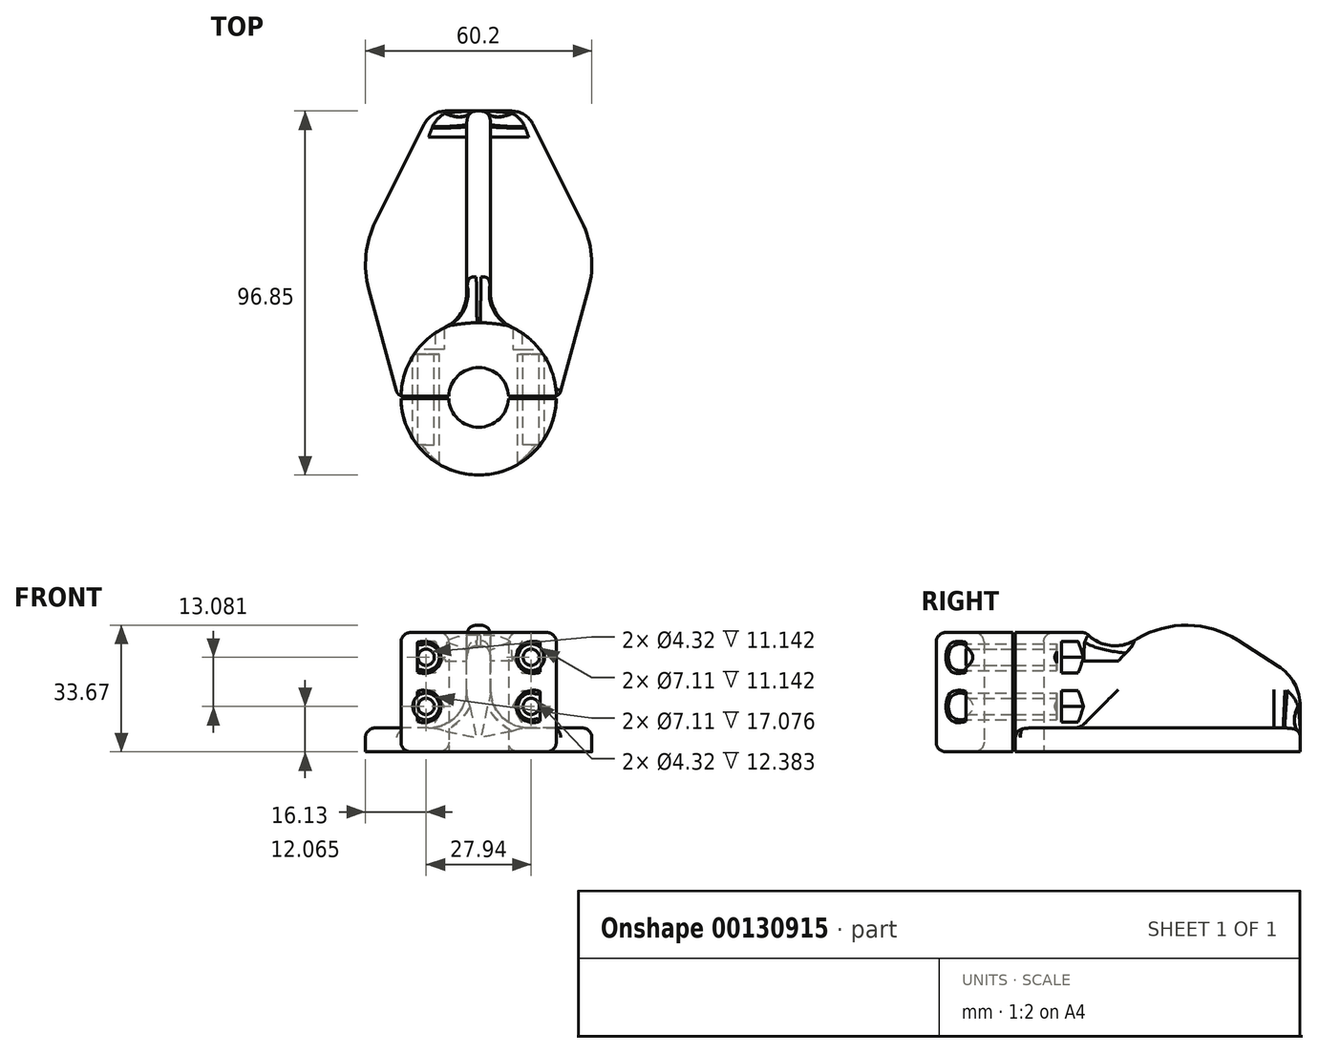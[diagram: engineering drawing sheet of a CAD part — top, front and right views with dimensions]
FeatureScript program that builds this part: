
annotation { "Feature Type Name" : "Feature", "Feature Type Description" : "" }
export const myFeature = defineFeature(function(context is Context, id is Id, definition is map)
    precondition{}
    {
        {
            var Q0;
            Q0=qCreatedBy(makeId("Top.planeOp"),FACE);
            var sketch = newSketch(context, id + "F0", { "sketchPlane" : qUnion([Q0])});
            skArc(sketch, "E0", {"start": v(-7.94, -0.32) * mm, "mid": v(0, -7.95) * mm, "end": v(7.94, -0.32) * mm});
            skLineSegment(sketch, "E1", {"start": v(51.79, -19.76) * mm, "end": v(0, -19.76) * mm});
            skLineSegment(sketch, "E2.MirrorCS", {"start": v(-51.79, -19.76) * mm, "end": v(0, -19.76) * mm});
            skArc(sketch, "E3", {"start": v(-20.65, -0.32) * mm, "mid": v(0, -20.65) * mm, "end": v(20.65, -0.32) * mm});
            skLineSegment(sketch, "E4", {"start": v(0, 76.2) * mm, "end": v(8.78, 76.2) * mm});
            skLineSegment(sketch, "E5", {"start": v(14.46, 72.69) * mm, "end": v(27.42, 46.77) * mm});
            skLineSegment(sketch, "E6", {"start": v(29.2, 28.75) * mm, "end": v(21.87, 1.72) * mm});
            skLineSegment(sketch, "E7", {"start": v(0, -19.76) * mm, "end": v(0, -61.3) * mm});
            skLineSegment(sketch, "E8.MirrorCS", {"start": v(0, 76.2) * mm, "end": v(-8.78, 76.2) * mm});
            skLineSegment(sketch, "E9.MirrorCS", {"start": v(-29.2, 28.75) * mm, "end": v(-21.87, 1.72) * mm});
            skLineSegment(sketch, "E10.MirrorCS", {"start": v(-14.46, 72.69) * mm, "end": v(-27.42, 46.77) * mm});
            skPoint(sketch, "E11.visualSharp", {"position": v(31.75, 38.1) * mm});
            skArc(sketch, "E11.filletArc", {"start": v(29.2, 28.75) * mm, "mid": v(29.97, 37.92) * mm, "end": v(27.42, 46.77) * mm});
            skPoint(sketch, "E12.visualSharp", {"position": v(-31.75, 38.1) * mm});
            skArc(sketch, "E12.filletArc", {"start": v(-27.42, 46.77) * mm, "mid": v(-29.97, 37.92) * mm, "end": v(-29.2, 28.75) * mm});
            skPoint(sketch, "E13.visualSharp", {"position": v(12.7, 76.2) * mm});
            skArc(sketch, "E13.filletArc", {"start": v(14.46, 72.69) * mm, "mid": v(12.11, 75.25) * mm, "end": v(8.78, 76.2) * mm});
            skPoint(sketch, "E14.visualSharp", {"position": v(-12.7, 76.2) * mm});
            skArc(sketch, "E14.filletArc", {"start": v(-8.78, 76.2) * mm, "mid": v(-12.11, 75.25) * mm, "end": v(-14.46, 72.69) * mm});
            skLineSegment(sketch, "E15", {"start": v(-24.66, 0) * mm, "end": v(25.12, 0) * mm});
            skLineSegment(sketch, "E16.0", {"start": v(-20.65, -0.32) * mm, "end": v(20.65, -0.32) * mm});
            skLineSegment(sketch, "E17.0", {"start": v(-20.03, 0.32) * mm, "end": v(20.03, 0.32) * mm});
            skArc(sketch, "E18.trimOffspring", {"start": v(7.94, 0.32) * mm, "mid": v(0, 7.95) * mm, "end": v(-7.94, 0.32) * mm});
            skArc(sketch, "E19.trimOffspring", {"start": v(20.65, 0.32) * mm, "mid": v(0, 20.65) * mm, "end": v(-20.65, 0.32) * mm});
            skPoint(sketch, "E20.visualSharp", {"position": v(-21.49, 0.32) * mm});
            skArc(sketch, "E20.filletArc", {"start": v(-21.87, 1.72) * mm, "mid": v(-21.19, 0.7) * mm, "end": v(-20.03, 0.32) * mm});
            skPoint(sketch, "E21.visualSharp", {"position": v(21.49, 0.32) * mm});
            skArc(sketch, "E21.filletArc", {"start": v(20.03, 0.32) * mm, "mid": v(21.19, 0.7) * mm, "end": v(21.87, 1.72) * mm});
            skSolve(sketch);
        }
        {
            var Q0;
            Q0=qCreatedBy(makeId("Right.planeOp"),FACE);
            var sketch = newSketch(context, id + "F1", { "sketchPlane" : qUnion([Q0])});
            skLineSegment(sketch, "E22", {"start": v(-14.29, 0) * mm, "end": v(-14.29, 19.05) * mm});
            skLineSegment(sketch, "E23", {"start": v(-14.29, 0) * mm, "end": v(76.2, 0) * mm});
            skPoint(sketch, "E24.visualSharp", {"position": v(46.35, 38.1) * mm});
            skLineSegment(sketch, "E25", {"start": v(76.2, 0) * mm, "end": v(76.2, 12.09) * mm});
            skLineSegment(sketch, "E26", {"start": v(70.33, 22.8) * mm, "end": v(59.54, 29.68) * mm});
            skLineSegment(sketch, "E27", {"start": v(-14.29, 19.05) * mm, "end": v(7.31, 19.05) * mm});
            skLineSegment(sketch, "E28", {"start": v(20.28, 22.61) * mm, "end": v(32.9, 30.1) * mm});
            skPoint(sketch, "E29.visualSharp", {"position": v(14.29, 19.05) * mm});
            skArc(sketch, "E29.filletArc", {"start": v(7.31, 19.05) * mm, "mid": v(14.04, 19.96) * mm, "end": v(20.28, 22.61) * mm});
            skPoint(sketch, "E30.visualSharp", {"position": v(46.36, 38.1) * mm});
            skArc(sketch, "E30.filletArc", {"start": v(59.54, 29.68) * mm, "mid": v(46.28, 33.67) * mm, "end": v(32.9, 30.1) * mm});
            skLineSegment(sketch, "E31", {"start": v(6.35, 0) * mm, "end": v(6.35, 19.05) * mm});
            skPoint(sketch, "E32.visualSharp", {"position": v(76.2, 19.05) * mm});
            skArc(sketch, "E32.filletArc", {"start": v(76.2, 12.09) * mm, "mid": v(74.64, 18.2) * mm, "end": v(70.33, 22.8) * mm});
            skSolve(sketch);
        }
        {
            var Q0;
            Q0=makeQuery(id+"F0.imprint","IMPRINT",FACE,{"disambiguationData":[TD([[makeQuery(id+"F0.imprint","IMPRINT",EDGE,{"derivedFrom":sQuery(id+"F0.wireOp",EDGE,"E0")}),-1.0]])]});
            var Q1;
            {var subQ1=sQuery(id+"F0.wireOp",EDGE,"E1");var subQ3=sQuery(id+"F0.wireOp",EDGE,"E3");var subQ4=makeQuery(id+"F0.imprint","INTERSECT",VERTEX,{"derivedFrom":[subQ1,subQ3]});Q1=makeQuery(id+"F0.imprint","IMPRINT",FACE,{"disambiguationData":[TD([[makeQuery(id+"F0.imprint","IMPRINT",EDGE,{"disambiguationData":[TD([[subQ4,1.0]])],"derivedFrom":subQ3}),1.0]])]});}
            var Q2;
            {var subQ1=sQuery(id+"F0.wireOp",EDGE,"E2.MirrorCS");var subQ3=sQuery(id+"F0.wireOp",EDGE,"E3");var subQ4=makeQuery(id+"F0.imprint","INTERSECT",VERTEX,{"derivedFrom":[subQ1,subQ3]});Q2=makeQuery(id+"F0.imprint","IMPRINT",FACE,{"disambiguationData":[TD([[makeQuery(id+"F0.imprint","IMPRINT",EDGE,{"disambiguationData":[TD([[subQ4,-1.0]])],"derivedFrom":subQ3}),1.0]])]});}
            extrude(context, id + "F2", {"entities" : qUnion([Q0, Q1, Q2]), "depth" : 31.75 * mm});
        }
        {
            var Q0;
            Q0=makeQuery(id+"F0.imprint","IMPRINT",FACE,{"disambiguationData":[TD([[makeQuery(id+"F0.imprint","IMPRINT",EDGE,{"derivedFrom":sQuery(id+"F0.wireOp",EDGE,"E4")}),-1.0]])]});
            extrude(context, id + "F3", {"entities" : qUnion([Q0]), "depth" : 6.35 * mm});
        }
        {
            var Q0;
            {var subQ3=sQuery(id+"F1.wireOp",EDGE,"E25");Q0=makeQuery(id+"F1.imprint","IMPRINT",FACE,{"disambiguationData":[TD([[makeQuery(id+"F1.imprint","IMPRINT",EDGE,{"derivedFrom":subQ3}),1.0]])]});}
            extrude(context, id + "F4", {"entities" : qUnion([Q0]), "depth" : 3.17 * mm, "hasSecondDirection" : true, "secondDirectionOppositeDirection" : true, "secondDirectionDepth" : 3.17 * mm});
        }
        {
            var Q0;
            {var subQ0=sQuery(id+"F0.wireOp",EDGE,"E18.trimOffspring");Q0=makeQuery(id+"F0.imprint","IMPRINT",FACE,{"disambiguationData":[TD([[makeQuery(id+"F0.imprint","IMPRINT",EDGE,{"derivedFrom":subQ0}),-1.0]])]});}
            extrude(context, id + "F5", {"entities" : qUnion([Q0]), "depth" : 31.75 * mm});
        }
        {
            var Q0;
            Q0=qCreatedBy(makeId("Front.planeOp"),FACE);
            var sketch = newSketch(context, id + "F6", { "sketchPlane" : qUnion([Q0])});
            skCircle(sketch, "E33", {"center": v(13.97, 12.07) * mm, "radius": 3.56 * mm});
            skCircle(sketch, "E34.cCircle", {"center": v(13.97, 12.07) * mm, "radius": 4.2 * mm, "construction": true});
            skLineSegment(sketch, "E34.0", {"start": v(11.55, 16.26) * mm, "end": v(16.39, 16.26) * mm});
            skLineSegment(sketch, "E34.1", {"start": v(16.39, 16.26) * mm, "end": v(18.8, 12.07) * mm});
            skLineSegment(sketch, "E34.2", {"start": v(18.8, 12.07) * mm, "end": v(16.39, 7.87) * mm});
            skLineSegment(sketch, "E34.3", {"start": v(16.39, 7.87) * mm, "end": v(11.55, 7.87) * mm});
            skLineSegment(sketch, "E34.4", {"start": v(11.55, 7.87) * mm, "end": v(9.13, 12.07) * mm});
            skLineSegment(sketch, "E34.5", {"start": v(9.13, 12.07) * mm, "end": v(11.55, 16.26) * mm});
            skPoint(sketch, "E34.0.midPoint", {"position": v(13.97, 16.26) * mm});
            skCircle(sketch, "E35", {"center": v(13.97, 12.07) * mm, "radius": 2.16 * mm});
            skLineSegment(sketch, "E36", {"start": v(0, 0) * mm, "end": v(0, 18.6) * mm});
            skLineSegment(sketch, "E37", {"start": v(0, 18.6) * mm, "end": v(28.99, 18.6) * mm});
            skPoint(sketch, "E38.MirrorP", {"position": v(13.97, 20.96) * mm});
            skLineSegment(sketch, "E39.MirrorCS", {"start": v(11.55, 29.34) * mm, "end": v(9.13, 25.15) * mm});
            skLineSegment(sketch, "E40.MirrorCS", {"start": v(16.39, 29.34) * mm, "end": v(11.55, 29.34) * mm});
            skLineSegment(sketch, "E41.MirrorCS", {"start": v(18.8, 25.15) * mm, "end": v(16.39, 29.34) * mm});
            skLineSegment(sketch, "E42.MirrorCS", {"start": v(11.55, 20.96) * mm, "end": v(16.39, 20.96) * mm});
            skLineSegment(sketch, "E43.MirrorCS", {"start": v(9.13, 25.15) * mm, "end": v(11.55, 20.96) * mm});
            skLineSegment(sketch, "E44.MirrorCS", {"start": v(16.39, 20.96) * mm, "end": v(18.8, 25.15) * mm});
            skCircle(sketch, "E45.MirrorC", {"center": v(13.97, 25.15) * mm, "radius": 2.16 * mm});
            skCircle(sketch, "E46.MirrorC", {"center": v(13.97, 25.15) * mm, "radius": 3.56 * mm});
            skCircle(sketch, "E47.MirrorC", {"center": v(13.97, 25.15) * mm, "radius": 4.2 * mm, "construction": true});
            skLineSegment(sketch, "E48.MirrorCS", {"start": v(-11.55, 16.26) * mm, "end": v(-16.39, 16.26) * mm});
            skLineSegment(sketch, "E49.MirrorCS", {"start": v(-16.39, 16.26) * mm, "end": v(-18.8, 12.07) * mm});
            skLineSegment(sketch, "E50.MirrorCS", {"start": v(-9.13, 25.15) * mm, "end": v(-11.55, 20.96) * mm});
            skCircle(sketch, "E51.MirrorC", {"center": v(-13.97, 25.15) * mm, "radius": 2.16 * mm});
            skCircle(sketch, "E52.MirrorC", {"center": v(-13.97, 25.15) * mm, "radius": 4.2 * mm, "construction": true});
            skLineSegment(sketch, "E53.MirrorCS", {"start": v(-16.39, 20.95) * mm, "end": v(-18.8, 25.15) * mm});
            skCircle(sketch, "E54.MirrorC", {"center": v(-13.97, 12.06) * mm, "radius": 2.16 * mm});
            skLineSegment(sketch, "E55.MirrorCS", {"start": v(-9.13, 12.07) * mm, "end": v(-11.55, 16.26) * mm});
            skLineSegment(sketch, "E56.MirrorCS", {"start": v(-11.55, 7.87) * mm, "end": v(-9.13, 12.06) * mm});
            skLineSegment(sketch, "E57.MirrorCS", {"start": v(-16.39, 7.87) * mm, "end": v(-11.55, 7.87) * mm});
            skCircle(sketch, "E58.MirrorC", {"center": v(-13.97, 12.06) * mm, "radius": 4.2 * mm, "construction": true});
            skPoint(sketch, "E59.MirrorP", {"position": v(-13.97, 16.26) * mm});
            skCircle(sketch, "E60.MirrorC", {"center": v(-13.97, 25.15) * mm, "radius": 3.56 * mm});
            skLineSegment(sketch, "E61.MirrorCS", {"start": v(-11.55, 29.34) * mm, "end": v(-9.13, 25.15) * mm});
            skLineSegment(sketch, "E62.MirrorCS", {"start": v(-18.8, 12.07) * mm, "end": v(-16.39, 7.87) * mm});
            skLineSegment(sketch, "E63.MirrorCS", {"start": v(-11.55, 20.96) * mm, "end": v(-16.39, 20.96) * mm});
            skPoint(sketch, "E64.MirrorP", {"position": v(-13.97, 20.96) * mm});
            skLineSegment(sketch, "E65.MirrorCS", {"start": v(-18.8, 25.15) * mm, "end": v(-16.39, 29.34) * mm});
            skLineSegment(sketch, "E66.MirrorCS", {"start": v(-16.39, 29.34) * mm, "end": v(-11.55, 29.34) * mm});
            skCircle(sketch, "E67.MirrorC", {"center": v(-13.97, 12.06) * mm, "radius": 3.56 * mm});
            skSolve(sketch);
        }
        {
            var Q0;
            Q0=makeQuery(id+"F6.imprint","IMPRINT",FACE,{"disambiguationData":[TD([[makeQuery(id+"F6.imprint","IMPRINT",EDGE,{"derivedFrom":sQuery(id+"F6.wireOp",EDGE,"E33")}),-1.0]])]});
            var Q1;
            Q1=makeQuery(id+"F6.imprint","IMPRINT",FACE,{"disambiguationData":[TD([[makeQuery(id+"F6.imprint","IMPRINT",EDGE,{"derivedFrom":sQuery(id+"F6.wireOp",EDGE,"E33")}),1.0]])]});
            var Q2;
            Q2=makeQuery(id+"F6.imprint","IMPRINT",FACE,{"disambiguationData":[TD([[makeQuery(id+"F6.imprint","IMPRINT",EDGE,{"derivedFrom":sQuery(id+"F6.wireOp",EDGE,"E35")}),1.0]])]});
            var Q3;
            Q3=makeQuery(id+"F6.imprint","IMPRINT",FACE,{"disambiguationData":[TD([[makeQuery(id+"F6.imprint","IMPRINT",EDGE,{"derivedFrom":sQuery(id+"F6.wireOp",EDGE,"E48.MirrorCS")}),1.0]])]});
            var Q4;
            Q4=makeQuery(id+"F6.imprint","IMPRINT",FACE,{"disambiguationData":[TD([[makeQuery(id+"F6.imprint","IMPRINT",EDGE,{"derivedFrom":sQuery(id+"F6.wireOp",EDGE,"E54.MirrorC")}),1.0]])]});
            var Q5;
            Q5=makeQuery(id+"F6.imprint","IMPRINT",FACE,{"disambiguationData":[TD([[makeQuery(id+"F6.imprint","IMPRINT",EDGE,{"derivedFrom":sQuery(id+"F6.wireOp",EDGE,"E54.MirrorC")}),-1.0]])]});
            var Q6;
            Q6=makeQuery(id+"F6.imprint","IMPRINT",FACE,{"disambiguationData":[TD([[makeQuery(id+"F6.imprint","IMPRINT",EDGE,{"derivedFrom":sQuery(id+"F6.wireOp",EDGE,"E50.MirrorCS")}),-1.0]])]});
            var Q7;
            Q7=makeQuery(id+"F6.imprint","IMPRINT",FACE,{"disambiguationData":[TD([[makeQuery(id+"F6.imprint","IMPRINT",EDGE,{"derivedFrom":sQuery(id+"F6.wireOp",EDGE,"E51.MirrorC")}),-1.0]])]});
            var Q8;
            Q8=makeQuery(id+"F6.imprint","IMPRINT",FACE,{"disambiguationData":[TD([[makeQuery(id+"F6.imprint","IMPRINT",EDGE,{"derivedFrom":sQuery(id+"F6.wireOp",EDGE,"E51.MirrorC")}),1.0]])]});
            var Q9;
            Q9=makeQuery(id+"F6.imprint","IMPRINT",FACE,{"disambiguationData":[TD([[makeQuery(id+"F6.imprint","IMPRINT",EDGE,{"derivedFrom":sQuery(id+"F6.wireOp",EDGE,"E39.MirrorCS")}),1.0]])]});
            var Q10;
            Q10=makeQuery(id+"F6.imprint","IMPRINT",FACE,{"disambiguationData":[TD([[makeQuery(id+"F6.imprint","IMPRINT",EDGE,{"derivedFrom":sQuery(id+"F6.wireOp",EDGE,"E45.MirrorC")}),1.0]])]});
            var Q11;
            Q11=makeQuery(id+"F6.imprint","IMPRINT",FACE,{"disambiguationData":[TD([[makeQuery(id+"F6.imprint","IMPRINT",EDGE,{"derivedFrom":sQuery(id+"F6.wireOp",EDGE,"E45.MirrorC")}),-1.0]])]});
            var Q12;
            Q12=makeQuery(id+"F6.imprint","IMPRINT",FACE,{"disambiguationData":[TD([[makeQuery(id+"F6.imprint","IMPRINT",EDGE,{"derivedFrom":sQuery(id+"F6.wireOp",EDGE,"E61.MirrorCS")}),1.0]])]});
            var Q13;
            Q13=makeQuery(id+"F6.imprint","IMPRINT",FACE,{"disambiguationData":[TD([[makeQuery(id+"F6.imprint","IMPRINT",EDGE,{"derivedFrom":sQuery(id+"F6.wireOp",EDGE,"E39.MirrorCS")}),-1.0]])]});
            var Q14;
            Q14=makeQuery(id+"F6.imprint","IMPRINT",FACE,{"disambiguationData":[TD([[makeQuery(id+"F6.imprint","IMPRINT",EDGE,{"derivedFrom":sQuery(id+"F6.wireOp",EDGE,"E34.0")}),1.0]])]});
            var Q15;
            Q15=makeQuery(id+"F6.imprint","IMPRINT",FACE,{"disambiguationData":[TD([[makeQuery(id+"F6.imprint","IMPRINT",EDGE,{"derivedFrom":sQuery(id+"F6.wireOp",EDGE,"E48.MirrorCS")}),-1.0]])]});
            extrude(context, id + "F7", {"entities" : qUnion([Q0, Q1, Q2, Q3, Q4, Q5, Q6, Q7, Q8, Q9, Q10, Q11, Q12, Q13, Q14, Q15]), "operationType" : NewBodyOperationType.REMOVE, "oppositeDirection" : true, "depth" : 30.43 * mm, "hasSecondDirection" : true, "secondDirectionOppositeDirection" : true, "secondDirectionDepth" : 12.7 * mm});
        }
        {
            var Q0;
            Q0=makeQuery(id+"F6.imprint","IMPRINT",FACE,{"disambiguationData":[TD([[makeQuery(id+"F6.imprint","IMPRINT",EDGE,{"derivedFrom":sQuery(id+"F6.wireOp",EDGE,"E33")}),1.0]])]});
            var Q1;
            Q1=makeQuery(id+"F6.imprint","IMPRINT",FACE,{"disambiguationData":[TD([[makeQuery(id+"F6.imprint","IMPRINT",EDGE,{"derivedFrom":sQuery(id+"F6.wireOp",EDGE,"E35")}),1.0]])]});
            var Q2;
            Q2=makeQuery(id+"F6.imprint","IMPRINT",FACE,{"disambiguationData":[TD([[makeQuery(id+"F6.imprint","IMPRINT",EDGE,{"derivedFrom":sQuery(id+"F6.wireOp",EDGE,"E54.MirrorC")}),1.0]])]});
            var Q3;
            Q3=makeQuery(id+"F6.imprint","IMPRINT",FACE,{"disambiguationData":[TD([[makeQuery(id+"F6.imprint","IMPRINT",EDGE,{"derivedFrom":sQuery(id+"F6.wireOp",EDGE,"E54.MirrorC")}),-1.0]])]});
            var Q4;
            Q4=makeQuery(id+"F6.imprint","IMPRINT",FACE,{"disambiguationData":[TD([[makeQuery(id+"F6.imprint","IMPRINT",EDGE,{"derivedFrom":sQuery(id+"F6.wireOp",EDGE,"E51.MirrorC")}),-1.0]])]});
            var Q5;
            Q5=makeQuery(id+"F6.imprint","IMPRINT",FACE,{"disambiguationData":[TD([[makeQuery(id+"F6.imprint","IMPRINT",EDGE,{"derivedFrom":sQuery(id+"F6.wireOp",EDGE,"E51.MirrorC")}),1.0]])]});
            var Q6;
            Q6=makeQuery(id+"F6.imprint","IMPRINT",FACE,{"disambiguationData":[TD([[makeQuery(id+"F6.imprint","IMPRINT",EDGE,{"derivedFrom":sQuery(id+"F6.wireOp",EDGE,"E45.MirrorC")}),1.0]])]});
            var Q7;
            Q7=makeQuery(id+"F6.imprint","IMPRINT",FACE,{"disambiguationData":[TD([[makeQuery(id+"F6.imprint","IMPRINT",EDGE,{"derivedFrom":sQuery(id+"F6.wireOp",EDGE,"E45.MirrorC")}),-1.0]])]});
            extrude(context, id + "F8", {"entities" : qUnion([Q0, Q1, Q2, Q3, Q4, Q5, Q6, Q7]), "operationType" : NewBodyOperationType.REMOVE, "depth" : 20.95 * mm, "hasSecondDirection" : true, "secondDirectionOppositeDirection" : false, "secondDirectionDepth" : 12.7 * mm});
        }
        {
            var Q0;
            Q0=makeQuery(id+"F6.imprint","IMPRINT",FACE,{"disambiguationData":[TD([[makeQuery(id+"F6.imprint","IMPRINT",EDGE,{"derivedFrom":sQuery(id+"F6.wireOp",EDGE,"E35")}),1.0]])]});
            var Q1;
            Q1=makeQuery(id+"F6.imprint","IMPRINT",FACE,{"disambiguationData":[TD([[makeQuery(id+"F6.imprint","IMPRINT",EDGE,{"derivedFrom":sQuery(id+"F6.wireOp",EDGE,"E54.MirrorC")}),-1.0]])]});
            var Q2;
            Q2=makeQuery(id+"F6.imprint","IMPRINT",FACE,{"disambiguationData":[TD([[makeQuery(id+"F6.imprint","IMPRINT",EDGE,{"derivedFrom":sQuery(id+"F6.wireOp",EDGE,"E51.MirrorC")}),1.0]])]});
            var Q3;
            Q3=makeQuery(id+"F6.imprint","IMPRINT",FACE,{"disambiguationData":[TD([[makeQuery(id+"F6.imprint","IMPRINT",EDGE,{"derivedFrom":sQuery(id+"F6.wireOp",EDGE,"E45.MirrorC")}),-1.0]])]});
            extrude(context, id + "F9", {"entities" : qUnion([Q0, Q1, Q2, Q3]), "depth" : 25.4 * mm, "hasSecondDirection" : true, "secondDirectionOppositeDirection" : true, "secondDirectionDepth" : 11.46 * mm});
        }
        {
            var Q0;
            Q0=makeQuery(id+"F3.opExtrude","SWEPT_BODY",BODY,{"disambiguationData":[OSD([sQuery(id+"F0.wireOp",EDGE,"E4"),sQuery(id+"F0.wireOp",EDGE,"E5"),sQuery(id+"F0.wireOp",EDGE,"E6"),sQuery(id+"F0.wireOp",EDGE,"E8.MirrorCS"),sQuery(id+"F0.wireOp",EDGE,"E9.MirrorCS"),sQuery(id+"F0.wireOp",EDGE,"E10.MirrorCS"),sQuery(id+"F0.wireOp",EDGE,"E11.filletArc"),sQuery(id+"F0.wireOp",EDGE,"E12.filletArc"),sQuery(id+"F0.wireOp",EDGE,"E13.filletArc"),sQuery(id+"F0.wireOp",EDGE,"E14.filletArc"),sQuery(id+"F0.wireOp",EDGE,"E19.trimOffspring"),sQuery(id+"F0.wireOp",EDGE,"E20.filletArc"),sQuery(id+"F0.wireOp",EDGE,"E21.filletArc")])]});
            var Q1;
            Q1=makeQuery(id+"F4.opExtrude","SWEPT_BODY",BODY,{"disambiguationData":[OSD([sQuery(id+"F1.wireOp",EDGE,"E23"),sQuery(id+"F1.wireOp",EDGE,"E25"),sQuery(id+"F1.wireOp",EDGE,"E26"),sQuery(id+"F1.wireOp",EDGE,"E27"),sQuery(id+"F1.wireOp",EDGE,"E28"),sQuery(id+"F1.wireOp",EDGE,"E29.filletArc"),sQuery(id+"F1.wireOp",EDGE,"E30.filletArc"),sQuery(id+"F1.wireOp",EDGE,"E31"),sQuery(id+"F1.wireOp",EDGE,"E32.filletArc")])]});
            var Q2;
            Q2=makeQuery(id+"F5.opExtrude","SWEPT_BODY",BODY,{"disambiguationData":[OSD([sQuery(id+"F0.wireOp",EDGE,"E17.0"),sQuery(id+"F0.wireOp",EDGE,"E18.trimOffspring"),sQuery(id+"F0.wireOp",EDGE,"E19.trimOffspring"),sQuery(id+"F0.wireOp",EDGE,"E20.filletArc"),sQuery(id+"F0.wireOp",EDGE,"E21.filletArc")])]});
            booleanBodies(context, id + "F10", {"operationType" : BooleanOperationType.UNION, "tools" : qUnion([Q0, Q1, Q2])});
        }
        {
            var Q0;
            {var subQ0=sQuery(id+"F0.wireOp",EDGE,"E18.trimOffspring");Q0=makeQuery(id+"F0.imprint","IMPRINT",FACE,{"disambiguationData":[TD([[makeQuery(id+"F0.imprint","IMPRINT",EDGE,{"derivedFrom":subQ0}),1.0]])]});}
            extrude(context, id + "F11", {"entities" : qUnion([Q0]), "operationType" : NewBodyOperationType.REMOVE, "depth" : 76.2 * mm});
        }
        {
            var Q0;
            Q0=makeQuery(id+"F2.opExtrude","CAP_EDGE",EDGE,{"disambiguationData":[OSD([sQuery(id+"F0.wireOp",EDGE,"E3")])],"isStart":false});
            var Q1;
            Q1=makeQuery(id+"F2.opExtrude","CAP_EDGE",EDGE,{"disambiguationData":[OSD([sQuery(id+"F0.wireOp",EDGE,"E0")])],"isStart":false});
            var Q2;
            Q2=makeQuery(id+"F5.opExtrude","CAP_EDGE",EDGE,{"disambiguationData":[OSD([sQuery(id+"F0.wireOp",EDGE,"E18.trimOffspring")])],"isStart":false});
            var Q3;
            Q3=makeQuery(id+"F5.opExtrude","CAP_EDGE",EDGE,{"disambiguationData":[OSD([sQuery(id+"F0.wireOp",EDGE,"E19.trimOffspring")])],"isStart":false});
            var Q4;
            Q4=makeQuery(id+"F4.opExtrude","CAP_EDGE",EDGE,{"disambiguationData":[OSD([sQuery(id+"F1.wireOp",EDGE,"E28")])],"isStart":false});
            var Q5;
            Q5=makeQuery(id+"F4.opExtrude","CAP_EDGE",EDGE,{"disambiguationData":[OSD([sQuery(id+"F1.wireOp",EDGE,"E28")])],"isStart":true});
            var Q6;
            Q6=makeQuery(id+"F3.opExtrude","CAP_EDGE",EDGE,{"disambiguationData":[OSD([sQuery(id+"F0.wireOp",EDGE,"E6")])],"isStart":false});
            var Q7;
            {var subQ1=sQuery(id+"F0.wireOp",EDGE,"E14.filletArc");var subQ2=sQuery(id+"F0.wireOp",EDGE,"E8.MirrorCS");var subQ3=sQuery(id+"F0.wireOp",EDGE,"E4");Q7=makeQuery(id+"F10.opBoolean","SPLIT",EDGE,{"disambiguationData":[TD([makeQuery(id+"F3.opExtrude","SWEPT_FACE",FACE,{"disambiguationData":[OSD([subQ1])]})])],"derivedFrom":makeQuery(id+"F3.opExtrude","CAP_EDGE",EDGE,{"disambiguationData":[OSD([subQ3,subQ2])],"isStart":false})});}
            var Q8;
            Q8=makeQuery(id+"F2.opExtrude","CAP_EDGE",EDGE,{"disambiguationData":[OSD([sQuery(id+"F0.wireOp",EDGE,"E3")])],"isStart":true});
            var Q9;
            Q9=makeQuery(id+"F2.opExtrude","CAP_EDGE",EDGE,{"disambiguationData":[OSD([sQuery(id+"F0.wireOp",EDGE,"E0")])],"isStart":true});
            fillet(context, id + "F12", {"entities" : qUnion([Q0, Q1, Q2, Q3, Q4, Q5, Q6, Q7, Q8, Q9]), "radius" : 2.54 * mm, "tangentPropagation" : true, "allowEdgeOverflow" : false});
        }
        {
            var Q0;
            {var subQ0=sQuery(id+"F0.wireOp",EDGE,"E19.trimOffspring");var subQ1=sQuery(id+"F0.wireOp",EDGE,"E21.filletArc");Q0=makeQuery(id+"F10.opBoolean","SPLIT",EDGE,{"disambiguationData":[TD([makeQuery(id+"F3.opExtrude","SWEPT_FACE",FACE,{"disambiguationData":[OSD([subQ1])]})])],"derivedFrom":makeQuery(id+"F3.opExtrude","CAP_EDGE",EDGE,{"disambiguationData":[OSD([subQ0])],"isStart":false})});}
            var Q1;
            Q1=makeQuery(id+"F10.opBoolean","INTERSECT",EDGE,{"derivedFrom":[makeQuery(id+"F3.opExtrude","CAP_FACE",FACE,{"disambiguationData":[OSD([sQuery(id+"F0.wireOp",EDGE,"E4"),sQuery(id+"F0.wireOp",EDGE,"E5"),sQuery(id+"F0.wireOp",EDGE,"E6"),sQuery(id+"F0.wireOp",EDGE,"E8.MirrorCS"),sQuery(id+"F0.wireOp",EDGE,"E9.MirrorCS"),sQuery(id+"F0.wireOp",EDGE,"E10.MirrorCS"),sQuery(id+"F0.wireOp",EDGE,"E11.filletArc"),sQuery(id+"F0.wireOp",EDGE,"E12.filletArc"),sQuery(id+"F0.wireOp",EDGE,"E13.filletArc"),sQuery(id+"F0.wireOp",EDGE,"E14.filletArc"),sQuery(id+"F0.wireOp",EDGE,"E19.trimOffspring"),sQuery(id+"F0.wireOp",EDGE,"E20.filletArc"),sQuery(id+"F0.wireOp",EDGE,"E21.filletArc")])],"isStart":false}),makeQuery(id+"F4.opExtrude","CAP_FACE",FACE,{"disambiguationData":[OSD([sQuery(id+"F1.wireOp",EDGE,"E23"),sQuery(id+"F1.wireOp",EDGE,"E25"),sQuery(id+"F1.wireOp",EDGE,"E26"),sQuery(id+"F1.wireOp",EDGE,"E27"),sQuery(id+"F1.wireOp",EDGE,"E28"),sQuery(id+"F1.wireOp",EDGE,"E29.filletArc"),sQuery(id+"F1.wireOp",EDGE,"E30.filletArc"),sQuery(id+"F1.wireOp",EDGE,"E31"),sQuery(id+"F1.wireOp",EDGE,"E32.filletArc")])],"isStart":false})]});
            var Q2;
            Q2=makeQuery(id+"F12.opFillet","BLEND_EDGE",EDGE,{"blendedFrom":[makeQuery(id+"F4.opExtrude","CAP_EDGE",EDGE,{"disambiguationData":[OSD([sQuery(id+"F1.wireOp",EDGE,"E28")])],"isStart":false}),makeQuery(id+"F5.opExtrude","SWEPT_FACE",FACE,{"disambiguationData":[OSD([sQuery(id+"F0.wireOp",EDGE,"E19.trimOffspring")])]})],"blendedInto":[makeQuery(id+"F5.opExtrude","SWEPT_FACE",FACE,{"disambiguationData":[OSD([sQuery(id+"F0.wireOp",EDGE,"E19.trimOffspring")])]})]});
            var Q3;
            {var subQ0=sQuery(id+"F0.wireOp",EDGE,"E19.trimOffspring");var subQ1=sQuery(id+"F0.wireOp",EDGE,"E20.filletArc");Q3=makeQuery(id+"F10.opBoolean","SPLIT",EDGE,{"disambiguationData":[TD([makeQuery(id+"F3.opExtrude","SWEPT_FACE",FACE,{"disambiguationData":[OSD([subQ1])]})])],"derivedFrom":makeQuery(id+"F3.opExtrude","CAP_EDGE",EDGE,{"disambiguationData":[OSD([subQ0])],"isStart":false})});}
            var Q4;
            Q4=makeQuery(id+"F10.opBoolean","INTERSECT",EDGE,{"derivedFrom":[makeQuery(id+"F3.opExtrude","CAP_FACE",FACE,{"disambiguationData":[OSD([sQuery(id+"F0.wireOp",EDGE,"E4"),sQuery(id+"F0.wireOp",EDGE,"E5"),sQuery(id+"F0.wireOp",EDGE,"E6"),sQuery(id+"F0.wireOp",EDGE,"E8.MirrorCS"),sQuery(id+"F0.wireOp",EDGE,"E9.MirrorCS"),sQuery(id+"F0.wireOp",EDGE,"E10.MirrorCS"),sQuery(id+"F0.wireOp",EDGE,"E11.filletArc"),sQuery(id+"F0.wireOp",EDGE,"E12.filletArc"),sQuery(id+"F0.wireOp",EDGE,"E13.filletArc"),sQuery(id+"F0.wireOp",EDGE,"E14.filletArc"),sQuery(id+"F0.wireOp",EDGE,"E19.trimOffspring"),sQuery(id+"F0.wireOp",EDGE,"E20.filletArc"),sQuery(id+"F0.wireOp",EDGE,"E21.filletArc")])],"isStart":false}),makeQuery(id+"F4.opExtrude","CAP_FACE",FACE,{"disambiguationData":[OSD([sQuery(id+"F1.wireOp",EDGE,"E23"),sQuery(id+"F1.wireOp",EDGE,"E25"),sQuery(id+"F1.wireOp",EDGE,"E26"),sQuery(id+"F1.wireOp",EDGE,"E27"),sQuery(id+"F1.wireOp",EDGE,"E28"),sQuery(id+"F1.wireOp",EDGE,"E29.filletArc"),sQuery(id+"F1.wireOp",EDGE,"E30.filletArc"),sQuery(id+"F1.wireOp",EDGE,"E31"),sQuery(id+"F1.wireOp",EDGE,"E32.filletArc")])],"isStart":true})]});
            fillet(context, id + "F13", {"entities" : qUnion([Q0, Q1, Q2, Q3, Q4]), "radius" : 10.16 * mm, "tangentPropagation" : true, "allowEdgeOverflow" : false});
        }
        {
            var Q0;
            Q0=makeQuery(id+"F8.boolean.opBoolean","INTERSECT",EDGE,{"derivedFrom":[makeQuery(id+"F2.opExtrude","SWEPT_FACE",FACE,{"disambiguationData":[OSD([sQuery(id+"F0.wireOp",EDGE,"E3")])]}),makeQuery(id+"F8.opExtrude","SWEPT_FACE",FACE,{"disambiguationData":[OSD([sQuery(id+"F6.wireOp",EDGE,"E46.MirrorC")])]})]});
            var Q1;
            Q1=makeQuery(id+"F8.boolean.opBoolean","INTERSECT",EDGE,{"derivedFrom":[makeQuery(id+"F2.opExtrude","SWEPT_FACE",FACE,{"disambiguationData":[OSD([sQuery(id+"F0.wireOp",EDGE,"E3")])]}),makeQuery(id+"F8.opExtrude","SWEPT_FACE",FACE,{"disambiguationData":[OSD([sQuery(id+"F6.wireOp",EDGE,"E33")])]})]});
            var Q2;
            Q2=makeQuery(id+"F8.boolean.opBoolean","INTERSECT",EDGE,{"derivedFrom":[makeQuery(id+"F2.opExtrude","SWEPT_FACE",FACE,{"disambiguationData":[OSD([sQuery(id+"F0.wireOp",EDGE,"E3")])]}),makeQuery(id+"F8.opExtrude","SWEPT_FACE",FACE,{"disambiguationData":[OSD([sQuery(id+"F6.wireOp",EDGE,"E67.MirrorC")])]})]});
            var Q3;
            Q3=makeQuery(id+"F8.boolean.opBoolean","INTERSECT",EDGE,{"derivedFrom":[makeQuery(id+"F2.opExtrude","SWEPT_FACE",FACE,{"disambiguationData":[OSD([sQuery(id+"F0.wireOp",EDGE,"E3")])]}),makeQuery(id+"F8.opExtrude","SWEPT_FACE",FACE,{"disambiguationData":[OSD([sQuery(id+"F6.wireOp",EDGE,"E60.MirrorC")])]})]});
            fillet(context, id + "F14", {"entities" : qUnion([Q0, Q1, Q2, Q3]), "radius" : 0.76 * mm, "tangentPropagation" : true, "allowEdgeOverflow" : false});
        }
        {
            var Q0;
            Q0=makeQuery(id+"F9.opExtrude","SWEPT_BODY",BODY,{"disambiguationData":[OSD([sQuery(id+"F6.wireOp",EDGE,"E51.MirrorC")])]});
            var Q1;
            Q1=makeQuery(id+"F9.opExtrude","SWEPT_BODY",BODY,{"disambiguationData":[OSD([sQuery(id+"F6.wireOp",EDGE,"E54.MirrorC")])]});
            var Q2;
            Q2=makeQuery(id+"F9.opExtrude","SWEPT_BODY",BODY,{"disambiguationData":[OSD([sQuery(id+"F6.wireOp",EDGE,"E35")])]});
            var Q3;
            Q3=makeQuery(id+"F9.opExtrude","SWEPT_BODY",BODY,{"disambiguationData":[OSD([sQuery(id+"F6.wireOp",EDGE,"E45.MirrorC")])]});
            var Q4;
            Q4=makeQuery(id+"F2.opExtrude","SWEPT_BODY",BODY,{"disambiguationData":[OSD([sQuery(id+"F0.wireOp",EDGE,"E0"),sQuery(id+"F0.wireOp",EDGE,"E3"),sQuery(id+"F0.wireOp",EDGE,"E16.0")])]});
            var Q5;
            Q5=makeQuery(id+"F3.opExtrude","SWEPT_BODY",BODY,{"disambiguationData":[OSD([sQuery(id+"F0.wireOp",EDGE,"E4"),sQuery(id+"F0.wireOp",EDGE,"E5"),sQuery(id+"F0.wireOp",EDGE,"E6"),sQuery(id+"F0.wireOp",EDGE,"E8.MirrorCS"),sQuery(id+"F0.wireOp",EDGE,"E9.MirrorCS"),sQuery(id+"F0.wireOp",EDGE,"E10.MirrorCS"),sQuery(id+"F0.wireOp",EDGE,"E11.filletArc"),sQuery(id+"F0.wireOp",EDGE,"E12.filletArc"),sQuery(id+"F0.wireOp",EDGE,"E13.filletArc"),sQuery(id+"F0.wireOp",EDGE,"E14.filletArc"),sQuery(id+"F0.wireOp",EDGE,"E19.trimOffspring"),sQuery(id+"F0.wireOp",EDGE,"E20.filletArc"),sQuery(id+"F0.wireOp",EDGE,"E21.filletArc")])]});
            booleanBodies(context, id + "F15", {"operationType" : BooleanOperationType.SUBTRACTION, "tools" : qUnion([Q0, Q1, Q2, Q3]), "targets" : qUnion([Q4, Q5])});
        }
    });
